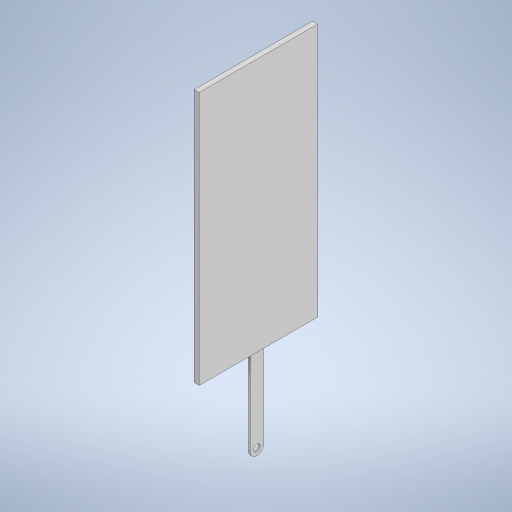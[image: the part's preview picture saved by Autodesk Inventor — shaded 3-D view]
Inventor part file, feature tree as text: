
AUTODESK INVENTOR PART (.ipt)
format: ipt  version: 2023 (Build 270158000, 158)  size: 239,104 bytes
history: native  units: mm
features: extrude x2, sketch x2, other x1
ambient origin geometry x8: Origin, YZ Plane, XZ Plane, XY Plane, X Axis, Y Axis, Z Axis, Center Point
bodies: Body1 (feature_tree)
feature tree (5):
  other  "Bryła1"
  extrude  "Wyciągnięcie proste1"  Depth=8.0mm
  extrude  "Wyciągnięcie proste2"  Depth=4.0mm
  sketch  "Szkic1"
  sketch  "Szkic2"
